# Revit family: Z-Niederhalter 80 mm, Loch 10.5 mm
name_source: partatom
category: HLS-Bauteile
revit_build: Autodesk Revit 2018 (Build: 20190510_1515(x64)
units: mm (PartAtom-declared; Revit-internal decimal feet)

## family parameters
Arbeitsebenenbasiert = Ja
Beim Laden mit Abzugskörper schneiden = Nein
Bemaßung runder Anschluss = Durchmesser verwenden
Gemeinsam genutzt = Ja
Immer vertikal = Nein
Raumberechnungspunkt = Nein
Teiletyp = Normal

## types (2) — shared parameters
Anzahl Befestigungsloch = 1 St
Befestigungsloch = 10.5 mm
Breite = 45 mm  [stored 0.147638 ft]
D = 11 mm
Fabrikat = MEFA
Firma = MEFA Befestigungs- und Montagesysteme GmbH
Gewicht = 0.10 kg
Gewicht pro Bauteil = 0.10 kg
Höhe = 15 mm
Kurztext2 = max. Plattenstärke 12 mm
L = 80 mm  [stored 0.262467 ft]
Länge = 80 mm  [stored 0.262467 ft]
MD = 3 mm  [stored 0.00984252 ft]
Material = Edelstahl
Stärke Material 1 = 3 mm
Vorgabe-Ansicht = 1219 mm
max. Plattenstärke = 12 mm
max. zul. Abhebelast (Paar) = 0.00 kN

## per-type parameters (varying)
| type | Artikelnummer | EAN | Kurztext1 | Materialname |
| Z Niederhalter 80, 1 Loch 10,5, V2A | 0779511 | 4250928418517 | Z-Niederhalter Gleitplatte V2A | V2A |
| Z Niederhalter 80, 1 Loch 10,5, V4A | 0779516 | 4250928418555 | Z-Niederhalter Gleitplatte V4A | V4A |

note: [stored X ft] marks values corroborated as IEEE doubles in the binary element streams (Revit-internal decimal feet)
